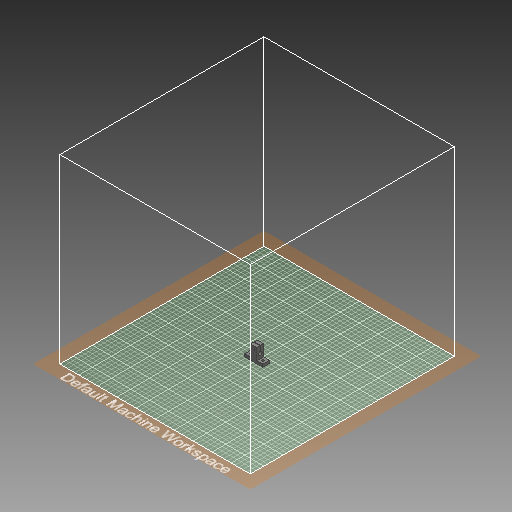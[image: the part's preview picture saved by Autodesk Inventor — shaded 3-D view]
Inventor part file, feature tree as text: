
AUTODESK INVENTOR PART (.ipt)
format: ipt  version: 2019 (Build 230136000, 136)  size: 346,624 bytes
history: native  units: in
note: dims shown in document units (in); Inventor stores cm internally (conversion verified against a paired STEP export)
features: sketch x9, extrude x8, other x3, reference x2
ambient origin geometry x8: Origin, YZ Plane, XZ Plane, XY Plane, X Axis, Y Axis, Z Axis, Center Point
bodies: Solid1 (feature_tree)
feature tree (22):
  extrude  "Extrusion1"  Depth=0.5906in
  extrude  "Extrusion2"  Depth=0.5512in
  extrude  "Extrusion4"  Depth=0.9843in
  extrude  "Extrusion5"  Depth=1.1811in TaperAngle=0.0deg
  extrude  "Extrusion6"  Depth=0.315in
  sketch  "Sketch7"  dims[d18=0.0394in d19=1.1811in d20=0.0in]
  sketch  "Sketch8"  dims[d21=0.1673in d22=0.2362in]
  extrude  "Extrusion8"  Depth=0.0394in TaperAngle=0.0deg
  extrude  "Extrusion9"  Depth=0.2362in
  sketch  "Sketch9"  dims[d23=1.1811in d24=0.0in d25=0.3937in]
  extrude  "Extrusion10"  Depth=0.3937in
  sketch  "Sketch1"  dims[d0=1.5748in d1=0.5906in]
  sketch  "Sketch2"  dims[d2=0.2362in d3=0.0in d4=0.5512in]
  sketch  "Sketch4"  dims[d5=0.9843in d6=0.0in d12=0.1673in]
  sketch  "Sketch5"  dims[d13=0.1673in d14=1.1811in d15=0.0in]
  sketch  "Sketch6"  dims[d16=0.315in d17=0.6299in]
  reference  "Reference1"
  reference  "Reference2"
  sketch  "Sketch10"  dims[d28=0.3937in d29=0.0in d30=0.3937in d31=0.0in d32=0.2362in d33=0.0591in d34=0.0in d35=0.2362in]
  other  "<userpath>\Stuff\Ajedrez2\Ajedrez2.iam"
  other  "Ajedrez2.iam"
  other  "Endstop mecânico - Chave fim de curso:2"
